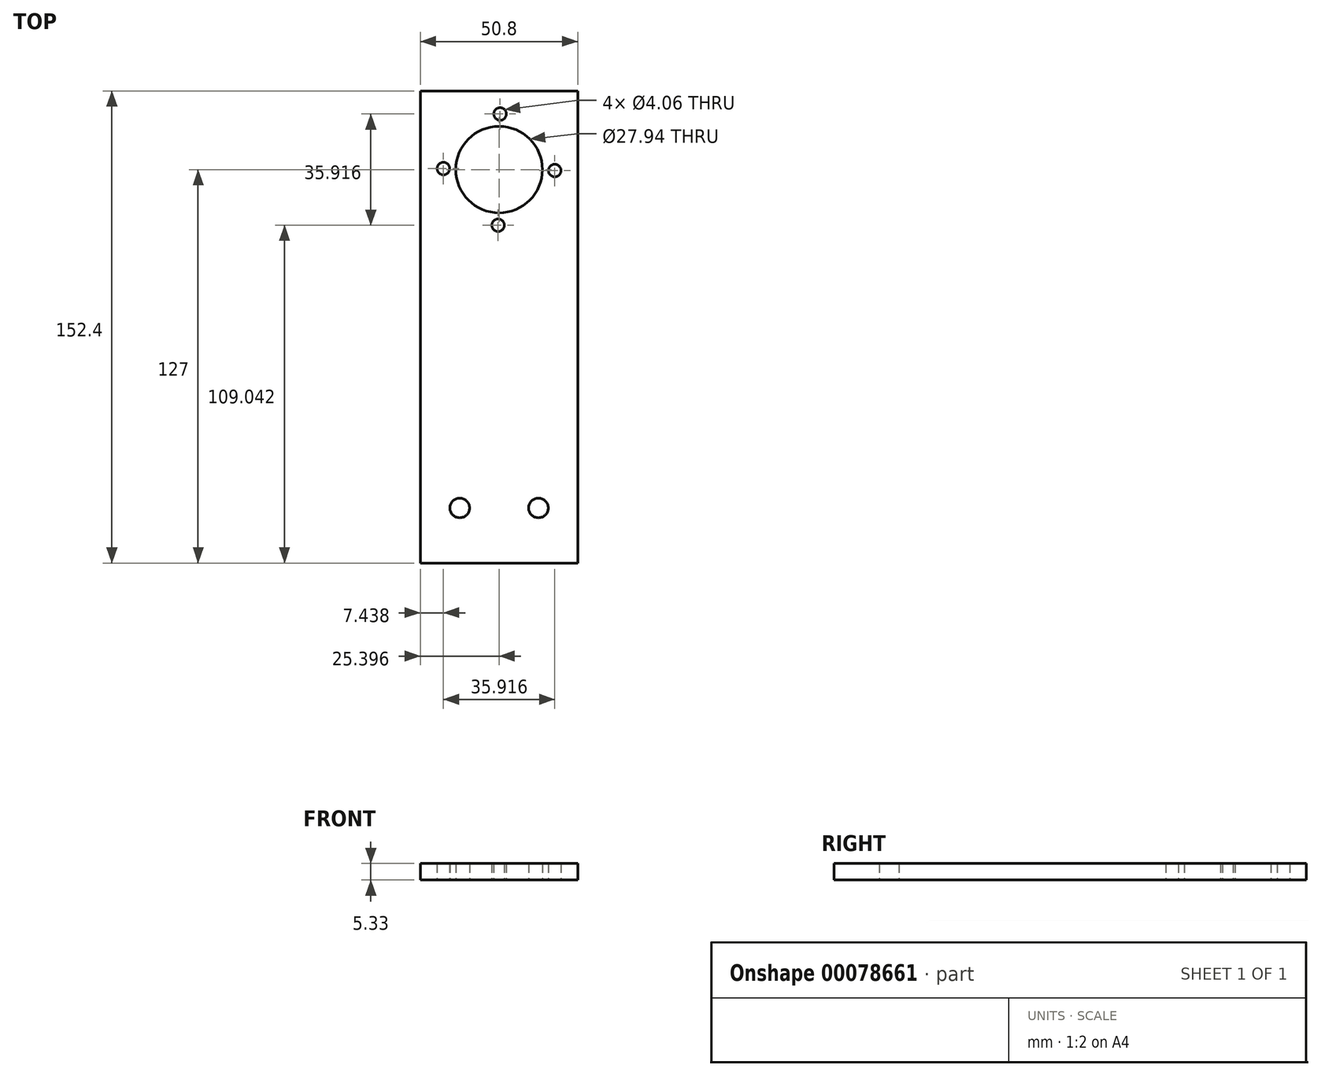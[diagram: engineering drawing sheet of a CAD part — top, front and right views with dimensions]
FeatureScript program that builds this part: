
annotation { "Feature Type Name" : "Feature", "Feature Type Description" : "" }
export const myFeature = defineFeature(function(context is Context, id is Id, definition is map)
    precondition{}
    {
        {
            var Q0;
            Q0=qCreatedBy(makeId("Top.planeOp"),FACE);
            var sketch = newSketch(context, id + "F0", { "sketchPlane" : qUnion([Q0])});
            skCircle(sketch, "E0", {"center": v(-17.73, 78.74) * mm, "radius": 2.03 * mm});
            skCircle(sketch, "E1.1.0", {"center": v(-36.01, 61.1) * mm, "radius": 2.03 * mm});
            skCircle(sketch, "E1.2.0", {"center": v(-18.38, 42.82) * mm, "radius": 2.03 * mm});
            skCircle(sketch, "E1.3.0", {"center": v(-0.1, 60.46) * mm, "radius": 2.03 * mm});
            skPoint(sketch, "E1.center", {"position": v(-18.05, 60.78) * mm});
            skCircle(sketch, "E2", {"center": v(-18.05, 60.78) * mm, "radius": 13.97 * mm});
            skLineSegment(sketch, "E3.top", {"start": v(7.35, 86.18) * mm, "end": v(-43.45, 86.18) * mm});
            skLineSegment(sketch, "E4.top", {"start": v(7.35, -66.22) * mm, "end": v(-43.45, -66.22) * mm});
            skLineSegment(sketch, "E5", {"start": v(7.35, 86.18) * mm, "end": v(7.35, -66.22) * mm});
            skLineSegment(sketch, "E6", {"start": v(-43.45, -66.22) * mm, "end": v(-43.45, 86.18) * mm});
            skCircle(sketch, "E7", {"center": v(-30.75, -48.44) * mm, "radius": 3.18 * mm});
            skCircle(sketch, "E8", {"center": v(-5.35, -48.44) * mm, "radius": 3.18 * mm});
            skSolve(sketch);
        }
        {
            var Q0;
            Q0 = qSketchRegion(id + "F0", true);
            extrude(context, id + "F1", {"entities" : qUnion([Q0]), "depth" : 5.33 * mm});
        }
        {
            var Q0;
            Q0=makeQuery(id+"F1.opExtrude","CAP_FACE",FACE,{"disambiguationData":[OSD([sQuery(id+"F0.wireOp",EDGE,"E0"),sQuery(id+"F0.wireOp",EDGE,"E1.1.0"),sQuery(id+"F0.wireOp",EDGE,"E1.2.0"),sQuery(id+"F0.wireOp",EDGE,"E1.3.0"),sQuery(id+"F0.wireOp",EDGE,"E2"),sQuery(id+"F0.wireOp",EDGE,"E3.top"),sQuery(id+"F0.wireOp",EDGE,"E4.top"),sQuery(id+"F0.wireOp",EDGE,"E5"),sQuery(id+"F0.wireOp",EDGE,"E6")])],"isStart":true});
            var sketch = newSketch(context, id + "F2", { "sketchPlane" : qUnion([Q0])});
            skCircle(sketch, "E9", {"center": v(-5.35, 48.44) * mm, "radius": 3.18 * mm});
            skCircle(sketch, "E10", {"center": v(-30.75, 48.44) * mm, "radius": 3.18 * mm});
            skSolve(sketch);
        }
        {
            var Q0;
            Q0 = qSketchRegion(id + "F2", true);
            extrude(context, id + "F3", {"entities" : qUnion([Q0]), "operationType" : NewBodyOperationType.REMOVE, "oppositeDirection" : true, "depth" : 25.4 * mm});
        }
    });
